# Revit family: DL-01
name_source: partatom
category: Осветительные приборы
revit_build: Autodesk Revit 2016 (Build: 20151007_0715(x64)
units: mm (PartAtom-declared; Revit-internal decimal feet)

## family parameters
Источник света = Да
Общий = Нет
Основа = Грань
При загрузке вырезать с полостями = Да
Размер круглого соединителя = Использовать диаметр
Тип детали = Нормальный
Точка расчета площади = Нет

## types (14) — shared parameters
ADSK_Единица измерения = Шт.
ADSK_Завод-изготовитель = ГК «Вартон»
ADSK_Количество фаз = 1
ADSK_Количество фаз числовое = 1
ADSK_Коэффициент мощности = 0.9
ADSK_Масса = 1.0833
ADSK_Напряжение = 220 В
ADSK_Номинальная мощность = 0 кВт
ADSK_Полная мощность = 0 кВ·А
ADSK_Ток = 0 А
ADSK_Энергоэффективность = 0 лм/Вт
IP Class = IP54
URL = http://varton.ru
Блок аварийного питания = Нет
Видимая форма излучения при визуализации = Нет
Группа модели = Светильники
Изготовитель = ГК «Вартон»
Класс Защиты = II
Класс пожароопасности = нет
Климатическая зона = УХЛ4
Корпус = ABS-пластик
Область использования = Рекомендован для освещения административных и торговых помещений
Плафон = Плафон самосвечение
Полная установленная мощность = 0 кВ·А
Разработчик = ООО ПРОРУБИМ
Разработчик (телефон) = +7 (495) 649-85-43
Разработчик модели (URL) = http://prorubim.com
Светофильтр = 16777215
Смещение цветовой температуры при затухании лампы = <Нет>
Тип ИС = LED
Угол наклона = -90.00°
Файл фотометрической сетки = V1-R0-01011-10000-4401130-33291.ies
zero-valued in all types: Отметка по умолчанию

## per-type parameters (varying)
| type | ADSK_Наименование | ADSK_Размер_Высота | ADSK_Размер_Длина | ADSK_Размер_Ширина | Излучение по длине прямоугольника | Излучение по ширине прямоугольника | Описание | Тип продукции |
| V1-R0-01011-10000-4401130 | Cветильник светодиодный ВАРТОН Downlight круглый встраиваемый 116 x 84 мм 11Вт 3000К | 84 мм | 116 мм | 116 мм | 116 мм | 116 мм | Cветильник светодиодный ВАРТОН Downlight круглый встраиваемый 116 x 84 мм 11Вт 3000К | Cветильник светодиодный ВАРТОН Downlight круглый встраиваемый 116 x 84 мм 11Вт 3000К |
| V1-R0-01011-10000-4401140 | Cветильник светодиодный ВАРТОН Downlight круглый встраиваемый 116 x 84 мм 11Вт 4000К | 84 мм | 116 мм | 116 мм | 116 мм | 116 мм | Cветильник светодиодный ВАРТОН Downlight круглый встраиваемый 116 x 84 мм 11Вт 4000К | Cветильник светодиодный ВАРТОН Downlight круглый встраиваемый 116 x 84 мм 11Вт 4000К |
| V1-R0-00083-10000-4401630 | Cветильник светодиодный ВАРТОН Downlight круглый встраиваемый 190 x 65 мм 16Вт 3000К | 65 мм | 190 мм | 190 мм | 190 мм | 190 мм | Cветильник светодиодный ВАРТОН Downlight круглый встраиваемый 190 x 65 мм 16Вт 3000К | Cветильник светодиодный ВАРТОН Downlight круглый встраиваемый 190 x 65 мм 16Вт 3000К |
| V1-R0-00083-10000-4401640 | Cветильник светодиодный ВАРТОН Downlight круглый встраиваемый 190 x 65 мм 16Вт 4000К | 65 мм | 190 мм | 190 мм | 190 мм | 190 мм | Cветильник светодиодный ВАРТОН Downlight круглый встраиваемый 190 x 65 мм 16Вт 4000К | Cветильник светодиодный ВАРТОН Downlight круглый встраиваемый 190 x 65 мм 16Вт 4000К |
| V1-R0-00083-10000-4402530 | Cветильник светодиодный ВАРТОН Downlight круглый встраиваемый 190 x 65 мм 25Вт 3000К | 65 мм | 190 мм | 190 мм | 190 мм | 190 мм | Cветильник светодиодный ВАРТОН Downlight круглый встраиваемый 190 x 65 мм 25Вт 3000К | Cветильник светодиодный ВАРТОН Downlight круглый встраиваемый 190 x 65 мм 25Вт 3000К |
| V1-R0-00083-10000-4402540 | Cветильник светодиодный ВАРТОН Downlight круглый встраиваемый 190 x 65 мм 25Вт 4000К | 65 мм | 190 мм | 190 мм | 190 мм | 190 мм | Cветильник светодиодный ВАРТОН Downlight круглый встраиваемый 190 x 65 мм 25Вт 4000К | Cветильник светодиодный ВАРТОН Downlight круглый встраиваемый 190 x 65 мм 25Вт 4000К |
| V1-R0-00084-10000-4404030 | Cветильник светодиодный ВАРТОН Downlight круглый встраиваемый 230 x 84 мм 40Вт 3000К | 84 мм | 230 мм | 230 мм | 230 мм | 230 мм | Cветильник светодиодный ВАРТОН Downlight круглый встраиваемый 230 x 84 мм 40Вт 3000К | Cветильник светодиодный ВАРТОН Downlight круглый встраиваемый 230 x 84 мм 40Вт 3000К |
| V1-R0-00084-10000-4404040 | Cветильник светодиодный ВАРТОН Downlight круглый встраиваемый 230 x 84 мм 40Вт 4000К | 84 мм | 230 мм | 230 мм | 230 мм | 230 мм | Cветильник светодиодный ВАРТОН Downlight круглый встраиваемый 230 x 84 мм 40Вт 4000К | Cветильник светодиодный ВАРТОН Downlight круглый встраиваемый 230 x 84 мм 40Вт 4000К |
| V1-R0-00083-10D01-4401630 | Cветильник светодиодный ВАРТОН Downlight круглый встраиваемый 190 x 65 мм 16Вт 3000К | 65 мм | 190 мм | 190 мм | 190 мм | 190 мм | Cветильник светодиодный ВАРТОН Downlight круглый встраиваемый 190 x 65 мм 16Вт 3000К | Cветильник светодиодный ВАРТОН Downlight круглый встраиваемый 190 x 65 мм 16Вт 3000К |
| V1-R0-00083-10D01-4401640 | Cветильник светодиодный ВАРТОН Downlight круглый встраиваемый 190 x 65 мм 16Вт 4000К | 65 мм | 190 мм | 190 мм | 190 мм | 190 мм | Cветильник светодиодный ВАРТОН Downlight круглый встраиваемый 190 x 65 мм 16Вт 4000К | Cветильник светодиодный ВАРТОН Downlight круглый встраиваемый 190 x 65 мм 16Вт 4000К |
| V1-R0-00083-10D01-4402530 | Cветильник светодиодный ВАРТОН Downlight круглый встраиваемый 190 x 65 мм 25Вт 3000К | 65 мм | 190 мм | 190 мм | 190 мм | 190 мм | Cветильник светодиодный ВАРТОН Downlight круглый встраиваемый 190 x 65 мм 25Вт 3000К | Cветильник светодиодный ВАРТОН Downlight круглый встраиваемый 190 x 65 мм 25Вт 3000К |
| V1-R0-00083-10D01-4402540 | Cветильник светодиодный ВАРТОН Downlight круглый встраиваемый 190 x 65 мм 25Вт 4000К | 65 мм | 190 мм | 190 мм | 190 мм | 190 мм | Cветильник светодиодный ВАРТОН Downlight круглый встраиваемый 190 x 65 мм 25Вт 4000К | Cветильник светодиодный ВАРТОН Downlight круглый встраиваемый 190 x 65 мм 25Вт 4000К |
| V1-R0-00084-10D01-4404030 | Cветильник светодиодный ВАРТОН Downlight круглый встраиваемый 230 x 69 мм 40Вт 3000К | 69 мм | 230 мм | 230 мм | 230 мм | 230 мм | Cветильник светодиодный ВАРТОН Downlight круглый встраиваемый 230 x 69 мм 40Вт 3000К | Cветильник светодиодный ВАРТОН Downlight круглый встраиваемый 230 x 69 мм 40Вт 3000К |
| V1-R0-00084-10D01-4404040 | Cветильник светодиодный ВАРТОН Downlight круглый встраиваемый 230 x 69 мм 40Вт 4000К | 69 мм | 230 мм | 230 мм | 230 мм | 230 мм | Cветильник светодиодный ВАРТОН Downlight круглый встраиваемый 230 x 69 мм 40Вт 4000К | Cветильник светодиодный ВАРТОН Downlight круглый встраиваемый 230 x 69 мм 40Вт 4000К |

note: column(s) folded — value = type name in every type: ADSK_Код изделия

## geometry (parser evidence)
native form markers: Blend x2
no freeform markers — native parametric forms only
